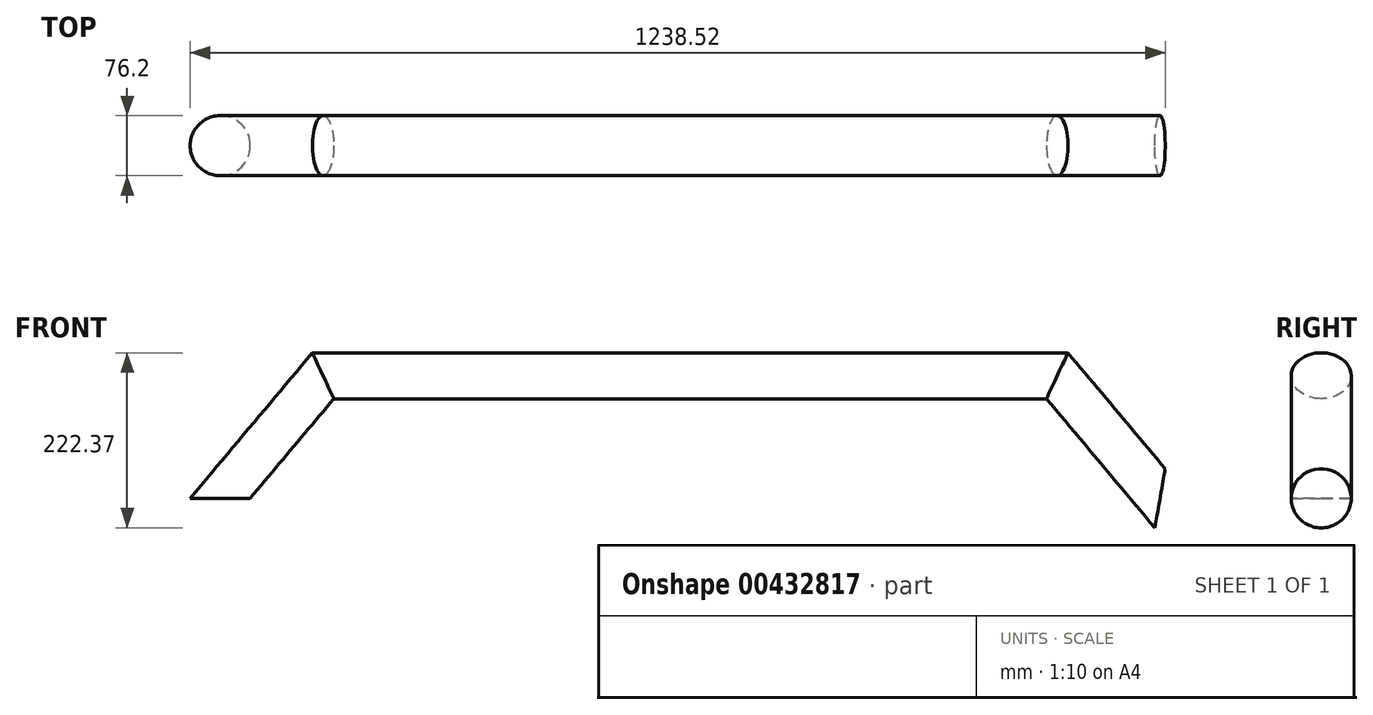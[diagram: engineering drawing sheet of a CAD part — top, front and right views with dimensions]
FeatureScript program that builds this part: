
annotation { "Feature Type Name" : "Feature", "Feature Type Description" : "" }
export const myFeature = defineFeature(function(context is Context, id is Id, definition is map)
    precondition{}
    {
        {
            var Q0;
            Q0=qCreatedBy(makeId("Top.planeOp"),FACE);
            var sketch = newSketch(context, id + "F0", { "sketchPlane" : qUnion([Q0])});
            skCircle(sketch, "E0", {"center": v(0, 0) * mm, "radius": 38.1 * mm});
            skSolve(sketch);
        }
        {
            var Q0;
            Q0=qCreatedBy(makeId("Front.planeOp"),FACE);
            var sketch = newSketch(context, id + "F1", { "sketchPlane" : qUnion([Q0])});
            skLineSegment(sketch, "E1", {"start": v(0, 0) * mm, "end": v(130.61, 155.66) * mm});
            skLineSegment(sketch, "E2", {"start": v(130.61, 155.66) * mm, "end": v(1063.19, 155.66) * mm});
            skLineSegment(sketch, "E3", {"start": v(1063.19, 155.66) * mm, "end": v(1193.8, 0) * mm});
            skSolve(sketch);
        }
        {
            var Q0;
            Q0=makeQuery(id+"F0.imprint","IMPRINT",FACE,{"disambiguationData":[TD([[makeQuery(id+"F0.imprint","IMPRINT",EDGE,{"derivedFrom":sQuery(id+"F0.wireOp",EDGE,"E0")}),1.0]])]});
            var Q1;
            Q1=sQuery(id+"F1.wireOp",EDGE,"E1");
            var Q2;
            Q2=sQuery(id+"F1.wireOp",EDGE,"E2");
            var Q3;
            Q3=sQuery(id+"F1.wireOp",EDGE,"E3");
            sweep(context, id + "F2", {"profiles" : qUnion([Q0]), "path" : qUnion([Q1, Q2, Q3])});
        }
    });
